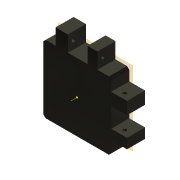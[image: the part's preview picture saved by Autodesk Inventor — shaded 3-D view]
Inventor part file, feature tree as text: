
AUTODESK INVENTOR PART (.ipt)
format: ipt  version: 2019 (Build 230136000, 136)  size: 131,584 bytes
history: native  units: mm
features: sketch x4, other x4, extrude x3, projected_geometry x2, plane x1, pattern_circular x1, reference x1
ambient origin geometry x8: Origin, YZ Plane, XZ Plane, XY Plane, X Axis, Y Axis, Z Axis, Center Point
bodies: Solid1 (feature_tree)
feature tree (16):
  plane  "Work Plane1"
  extrude  "Extrusion1"  Depth=14.0mm TaperAngle=0.0deg
  sketch  "Sketch2"  dims[d4=3.0mm d5=14.0mm d6=0.0mm]
  extrude  "Extrusion2"  Depth=14.0mm TaperAngle=0.0deg
  extrude  "Extrusion3"  [1 undecoded]
  other  "Work Axis1"
  pattern_circular  "Circular Pattern1"  [2 undecoded]
  sketch  "Sketch1"  dims[d0=16.0mm d1=0.0mm d2=14.0mm d3=0.0mm]
  reference  "Reference1"
  sketch  "Sketch3"  dims[d7=20.0mm d8=90.0deg]
  projected_geometry  "Projected Loop1"
  sketch  "Sketch4"
  projected_geometry  "Projected Loop2"
  other  "00_XY_stage-CHUO_SEIKI_LD-647-R1.iam"
  other  "00_XY_stage-CHUO_SEIKI_LD-647-R1-Top:1"
  other  "Assembly2"
note: 3 required parameter values undecoded (feature->parameter linkage not recoverable at this tier; creation-order binding heuristic only, values carry confidence <= 0.55)
